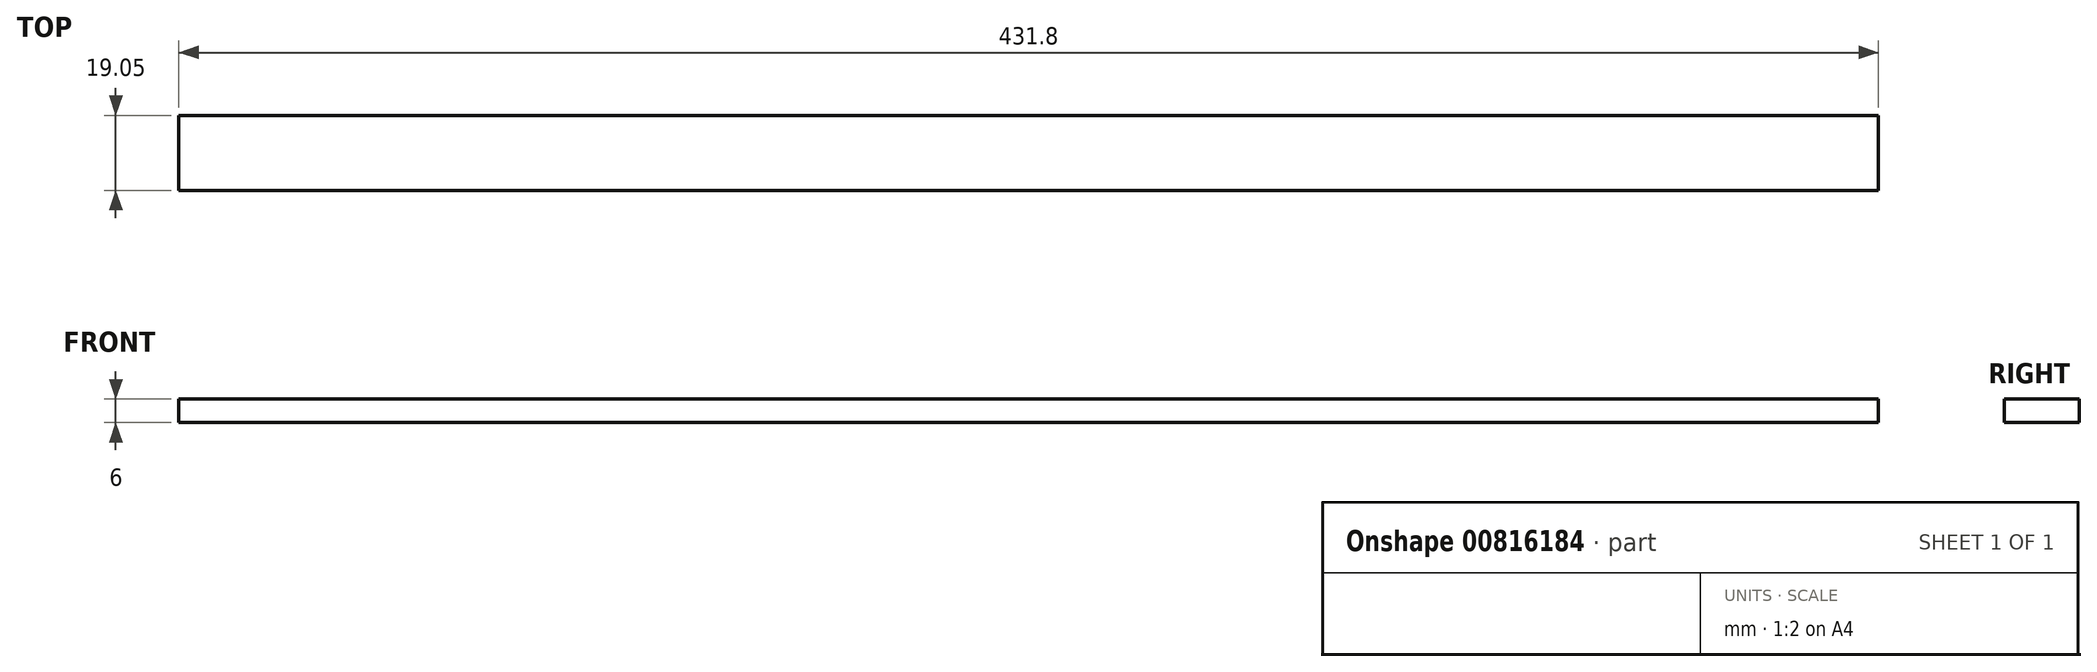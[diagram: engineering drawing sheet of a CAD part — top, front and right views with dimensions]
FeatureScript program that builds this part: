
annotation { "Feature Type Name" : "Feature", "Feature Type Description" : "" }
export const myFeature = defineFeature(function(context is Context, id is Id, definition is map)
    precondition{}
    {
        {
            var Q0;
            Q0=qCreatedBy(makeId("Top.planeOp"),FACE);
            var sketch = newSketch(context, id + "F0", { "sketchPlane" : qUnion([Q0])});
            skLineSegment(sketch, "E0.bottom", {"start": v(143.92, -54.24) * mm, "end": v(-287.88, -54.24) * mm});
            skLineSegment(sketch, "E0.top", {"start": v(143.92, -35.2) * mm, "end": v(-287.88, -35.2) * mm});
            skLineSegment(sketch, "E0.left", {"start": v(143.92, -54.24) * mm, "end": v(143.92, -35.2) * mm});
            skLineSegment(sketch, "E0.right", {"start": v(-287.88, -54.24) * mm, "end": v(-287.88, -35.2) * mm});
            skPoint(sketch, "E0.middle", {"position": v(-71.98, -44.72) * mm});
            skSolve(sketch);
        }
        {
            var Q0;
            Q0 = qSketchRegion(id + "F0", true);
            extrude(context, id + "F1", {"entities" : qUnion([Q0]), "endBound" : BoundingType.SYMMETRIC, "depth" : 6 * mm, "offsetDistance" : 25 * mm});
        }
    });
